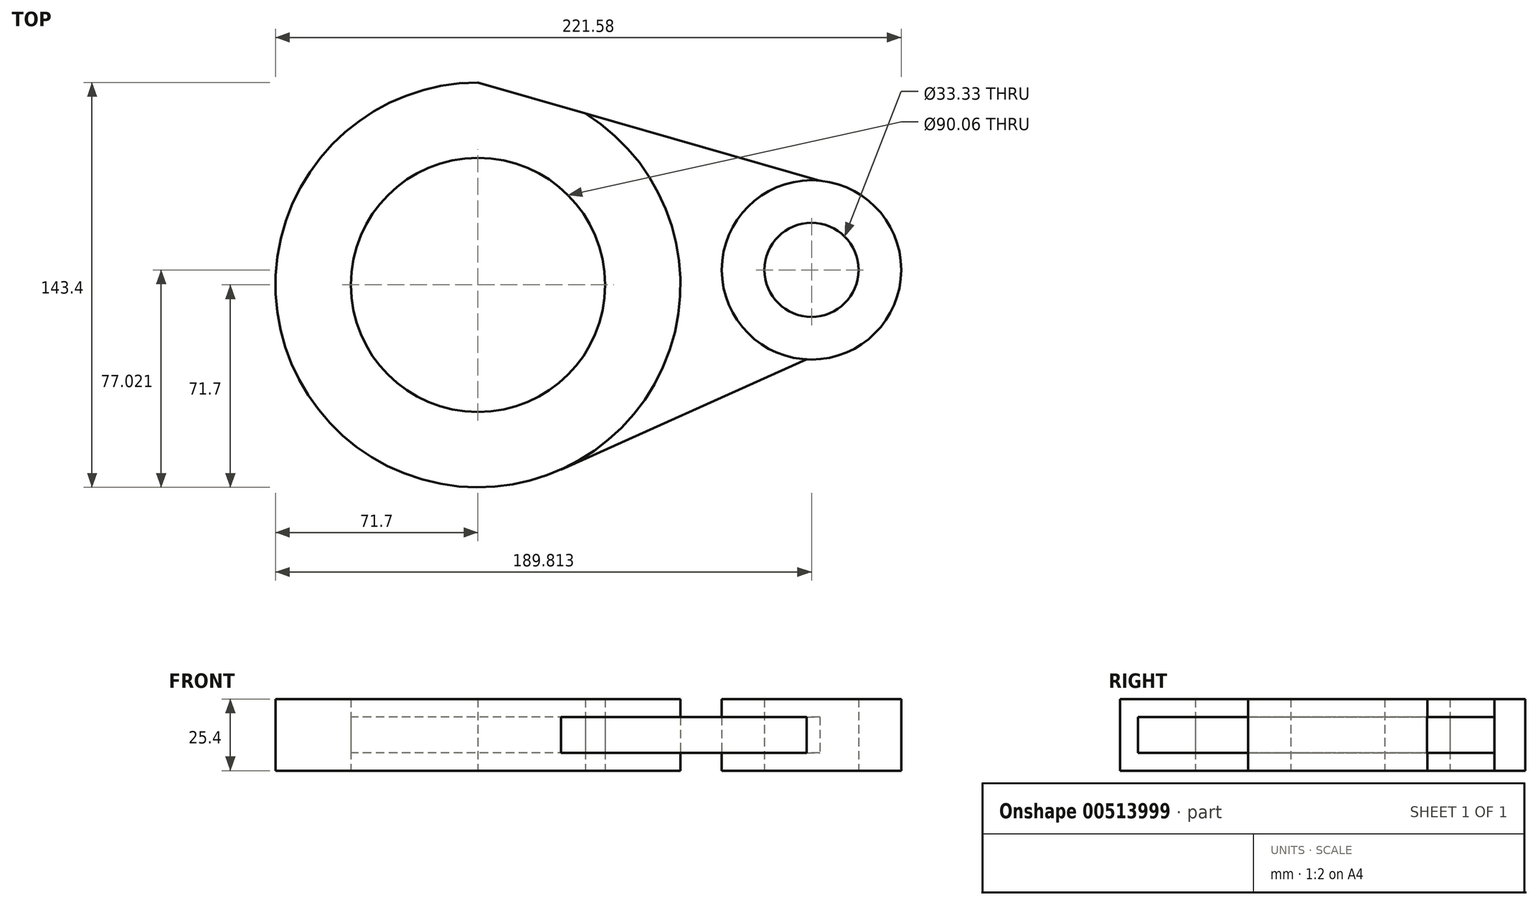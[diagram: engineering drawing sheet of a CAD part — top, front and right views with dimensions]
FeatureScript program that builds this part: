
annotation { "Feature Type Name" : "Feature", "Feature Type Description" : "" }
export const myFeature = defineFeature(function(context is Context, id is Id, definition is map)
    precondition{}
    {
        {
            var Q0;
            Q0=qCreatedBy(makeId("Top.planeOp"),FACE);
            var sketch = newSketch(context, id + "F0", { "sketchPlane" : qUnion([Q0])});
            skCircle(sketch, "E0", {"center": v(0, 0) * mm, "radius": 71.7 * mm});
            skCircle(sketch, "E1", {"center": v(0, 0) * mm, "radius": 45.03 * mm});
            skCircle(sketch, "E2", {"center": v(118.11, 5.32) * mm, "radius": 31.77 * mm});
            skCircle(sketch, "E3", {"center": v(118.11, 5.32) * mm, "radius": 16.66 * mm});
            skLineSegment(sketch, "E4", {"start": v(0, 71.7) * mm, "end": v(121.08, 36.95) * mm});
            skLineSegment(sketch, "E5", {"start": v(116.39, -26.4) * mm, "end": v(29.34, -65.43) * mm});
            skSolve(sketch);
        }
        {
            var Q0;
            Q0=makeQuery(id+"F0.imprint","IMPRINT",FACE,{"disambiguationData":[TD([[makeQuery(id+"F0.imprint","IMPRINT",EDGE,{"derivedFrom":sQuery(id+"F0.wireOp",EDGE,"E1")}),-1.0]])]});
            var Q1;
            Q1=makeQuery(id+"F0.imprint","IMPRINT",FACE,{"disambiguationData":[TD([[makeQuery(id+"F0.imprint","IMPRINT",EDGE,{"derivedFrom":sQuery(id+"F0.wireOp",EDGE,"E3")}),-1.0]])]});
            extrude(context, id + "F1", {"entities" : qUnion([Q0, Q1]), "endBound" : BoundingType.SYMMETRIC, "depth" : 25.4 * mm});
        }
        {
            var Q0;
            Q0=makeQuery(id+"F0.imprint","IMPRINT",FACE,{"disambiguationData":[TD([[makeQuery(id+"F0.imprint","IMPRINT",EDGE,{"derivedFrom":sQuery(id+"F0.wireOp",EDGE,"E1")}),1.0]])]});
            var Q1;
            {var subQ0=sQuery(id+"F0.wireOp",EDGE,"E5");Q1=makeQuery(id+"F0.imprint","IMPRINT",FACE,{"disambiguationData":[TD([[makeQuery(id+"F0.imprint","IMPRINT",EDGE,{"derivedFrom":subQ0}),-1.0]])]});}
            extrude(context, id + "F2", {"entities" : qUnion([Q0, Q1]), "endBound" : BoundingType.SYMMETRIC, "depth" : 12.7 * mm});
        }
    });
